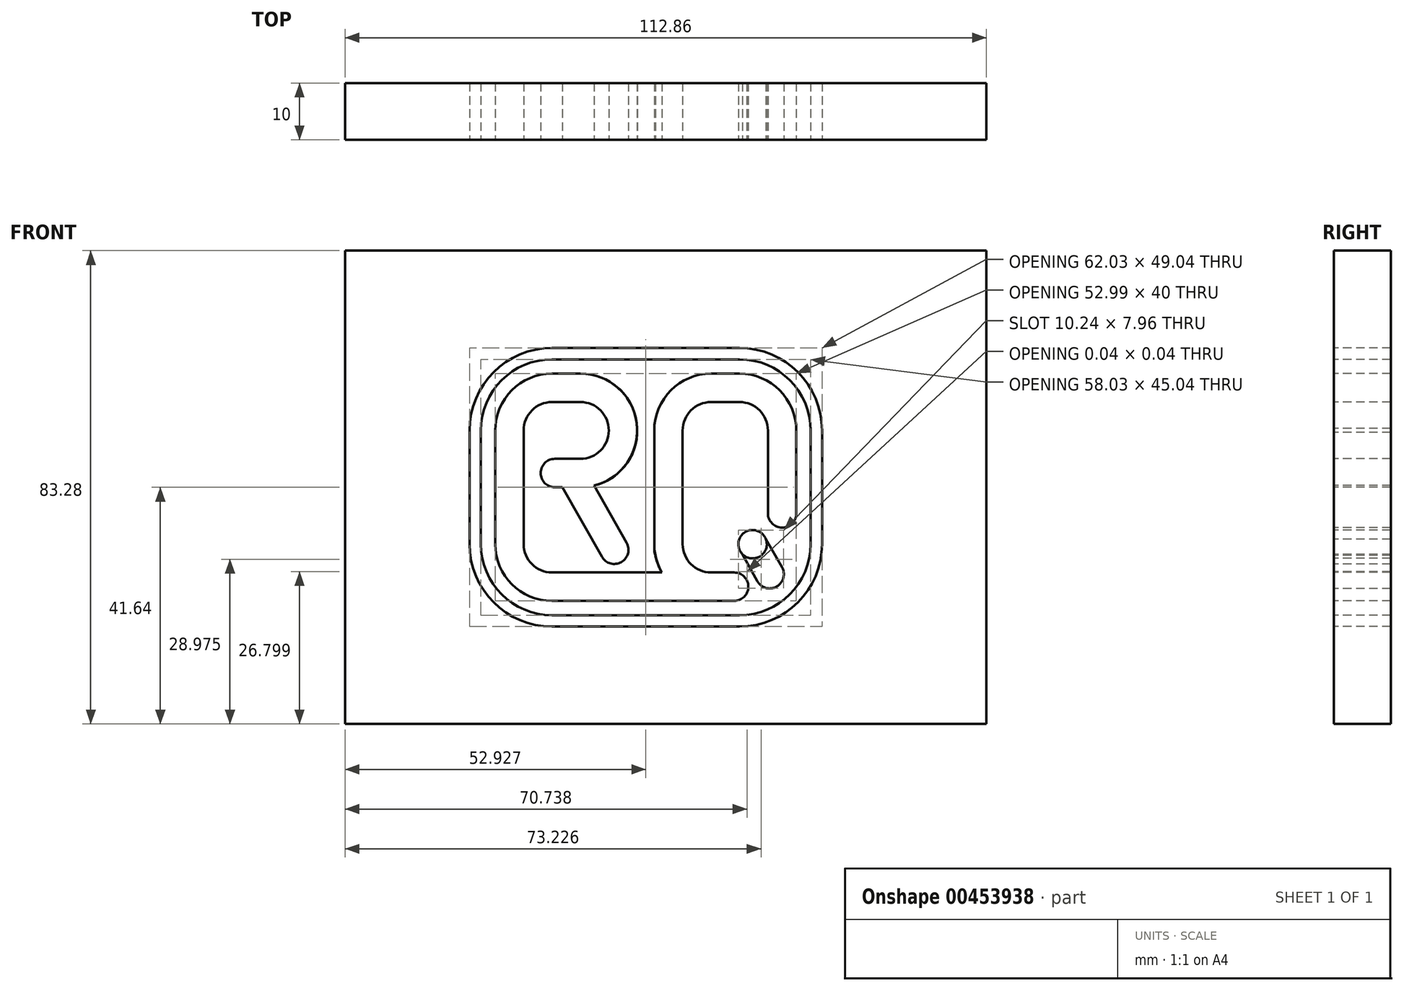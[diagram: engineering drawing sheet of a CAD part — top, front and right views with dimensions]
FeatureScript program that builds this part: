
annotation { "Feature Type Name" : "Feature", "Feature Type Description" : "" }
export const myFeature = defineFeature(function(context is Context, id is Id, definition is map)
    precondition{}
    {
        {
            var Q0;
            Q0=qCreatedBy(makeId("Front.planeOp"),FACE);
            var sketch = newSketch(context, id + "F0", { "sketchPlane" : qUnion([Q0])});
            skPoint(sketch, "E0.middle", {"position": v(0, 0) * mm});
            skLineSegment(sketch, "E1", {"start": v(-25, 10) * mm, "end": v(-25, -10) * mm});
            skLineSegment(sketch, "E2", {"start": v(-2, -20) * mm, "end": v(-0.38, -20) * mm});
            skLineSegment(sketch, "E3", {"start": v(-2, -11) * mm, "end": v(-2, 10) * mm});
            skLineSegment(sketch, "E4", {"start": v(8, 20) * mm, "end": v(13, 20) * mm});
            skLineSegment(sketch, "E5", {"start": v(23, 10) * mm, "end": v(23, -10) * mm});
            skLineSegment(sketch, "E6", {"start": v(13, -20) * mm, "end": v(9, -20) * mm});
            skLineSegment(sketch, "E7", {"start": v(-25, 20) * mm, "end": v(-15, 20) * mm});
            skLineSegment(sketch, "E8", {"start": v(-19.5, 0) * mm, "end": v(-15, 0) * mm});
            skLineSegment(sketch, "E9", {"start": v(-5, 10.33) * mm, "end": v(-5, 10.33) * mm});
            skPoint(sketch, "E10.visualSharp", {"position": v(-5.33, 20) * mm});
            skArc(sketch, "E10.filletArc", {"start": v(-5, 10.33) * mm, "mid": v(-8.05, 17.19) * mm, "end": v(-15, 20) * mm});
            skArc(sketch, "E11.filletArc", {"start": v(-15, 0) * mm, "mid": v(-7.81, 3.05) * mm, "end": v(-5, 10.33) * mm});
            skPoint(sketch, "E12.visualSharp", {"position": v(-3.63, -20) * mm});
            skPoint(sketch, "E13.visualSharp", {"position": v(23, -20) * mm});
            skPoint(sketch, "E14.visualSharp", {"position": v(23, 20) * mm});
            skArc(sketch, "E14.filletArc", {"start": v(23, 10) * mm, "mid": v(20.07, 17.07) * mm, "end": v(13, 20) * mm});
            skPoint(sketch, "E15.visualSharp", {"position": v(-2, 20) * mm});
            skArc(sketch, "E15.filletArc", {"start": v(8, 20) * mm, "mid": v(0.92, 17.07) * mm, "end": v(-2, 10) * mm});
            skPoint(sketch, "E16.visualSharp", {"position": v(-2, -20) * mm});
            skArc(sketch, "E17.0", {"start": v(8, 15) * mm, "mid": v(4.46, 13.54) * mm, "end": v(3, 10) * mm});
            skLineSegment(sketch, "E17.1", {"start": v(3, -11) * mm, "end": v(3, 10) * mm});
            skLineSegment(sketch, "E17.2", {"start": v(8, 15) * mm, "end": v(13, 15) * mm});
            skArc(sketch, "E17.4", {"start": v(18, 10) * mm, "mid": v(16.53, 13.54) * mm, "end": v(13, 15) * mm});
            skLineSegment(sketch, "E17.5", {"start": v(18, 10) * mm, "end": v(18, -10) * mm});
            skArc(sketch, "E17.6", {"start": v(14.29, -14.83) * mm, "mid": v(14.3, -14.82) * mm, "end": v(14.33, -14.82) * mm});
            skLineSegment(sketch, "E17.7", {"start": v(13, -15) * mm, "end": v(9, -15) * mm});
            skArc(sketch, "E18.1", {"start": v(-15, 5) * mm, "mid": v(-11.44, 6.5) * mm, "end": v(-10, 10.08) * mm});
            skArc(sketch, "E18.2", {"start": v(-10, 10.08) * mm, "mid": v(-11.5, 13.56) * mm, "end": v(-15, 15) * mm});
            skLineSegment(sketch, "E18.3", {"start": v(-20, 15) * mm, "end": v(-15, 15) * mm});
            skLineSegment(sketch, "E19.0", {"start": v(-30, 17.5) * mm, "end": v(-30, -10) * mm});
            skLineSegment(sketch, "E20.0", {"start": v(-1, -15) * mm, "end": v(-0.38, -15) * mm});
            skLineSegment(sketch, "E21", {"start": v(-20, -20) * mm, "end": v(-2, -20) * mm});
            skLineSegment(sketch, "E22", {"start": v(-1, -15) * mm, "end": v(0, -15) * mm});
            skLineSegment(sketch, "E23.0", {"start": v(-20, -15) * mm, "end": v(0, -15) * mm});
            skLineSegment(sketch, "E24", {"start": v(-5, 10.33) * mm, "end": v(-5, 0) * mm});
            skLineSegment(sketch, "E25", {"start": v(0.5, -13.5) * mm, "end": v(0.5, -13.5) * mm});
            skPoint(sketch, "E26.visualSharp", {"position": v(3, -13.5) * mm});
            skArc(sketch, "E26.filletArc", {"start": v(0.5, -13.5) * mm, "mid": v(2.26, -12.77) * mm, "end": v(3, -11) * mm, "construction": true});
            skPoint(sketch, "E27.newPointB", {"position": v(-23.5, -13.5) * mm});
            skArc(sketch, "E27.filletArc", {"start": v(-2, -11) * mm, "mid": v(-1.27, -12.77) * mm, "end": v(0.5, -13.5) * mm});
            skPoint(sketch, "E28.visualSharp", {"position": v(-30, -20) * mm});
            skArc(sketch, "E28.filletArc", {"start": v(-30, -19.5) * mm, "mid": v(-29.85, -19.85) * mm, "end": v(-29.5, -20) * mm});
            skLineSegment(sketch, "E29", {"start": v(-7.28, -12.77) * mm, "end": v(-7.28, -12.77) * mm});
            skArc(sketch, "E30.filletArc", {"start": v(-7.28, -12.77) * mm, "mid": v(-6.55, -11) * mm, "end": v(-7.27, -9.24) * mm});
            skArc(sketch, "E31.filletArc", {"start": v(-11.23, -12.21) * mm, "mid": v(-9.4, -13.48) * mm, "end": v(-7.28, -12.77) * mm});
            skLineSegment(sketch, "E32.0", {"start": v(14.32, -14.86) * mm, "end": v(14.29, -14.83) * mm});
            skPoint(sketch, "E33.newPointB", {"position": v(-25, 20) * mm});
            skPoint(sketch, "E34.visualSharp", {"position": v(-23.5, 5) * mm});
            skPoint(sketch, "E35.visualSharp", {"position": v(-23.5, 0) * mm});
            skLineSegment(sketch, "E36", {"start": v(-30, 10) * mm, "end": v(-30, 17.5) * mm});
            skLineSegment(sketch, "E37", {"start": v(-20, 20) * mm, "end": v(-25, 20) * mm});
            skPoint(sketch, "E38.visualSharp", {"position": v(-30, 20) * mm});
            skArc(sketch, "E38.filletArc", {"start": v(-20, 20) * mm, "mid": v(-27.07, 17.07) * mm, "end": v(-30, 10) * mm});
            skPoint(sketch, "E39", {"position": v(19.6, -17.6) * mm});
            skPoint(sketch, "E40.orphan", {"position": v(17, -13) * mm});
            skLineSegment(sketch, "E41.trimOffspring", {"start": v(13, -20) * mm, "end": v(-0.38, -20) * mm});
            skPoint(sketch, "E42.newPointB", {"position": v(-25, -20) * mm});
            skArc(sketch, "E42.filletArc", {"start": v(-25, -10) * mm, "mid": v(-23.54, -13.54) * mm, "end": v(-20, -15) * mm});
            skLineSegment(sketch, "E43", {"start": v(-15, 20) * mm, "end": v(8, 20) * mm});
            skLineSegment(sketch, "E44", {"start": v(21.86, -24.52) * mm, "end": v(-20, -24.52) * mm});
            skLineSegment(sketch, "E45", {"start": v(27.51, -22.02) * mm, "end": v(27.51, -18.86) * mm});
            skLineSegment(sketch, "E46", {"start": v(13, 24.52) * mm, "end": v(-20, 24.52) * mm});
            skLineSegment(sketch, "E47", {"start": v(-34.52, -10) * mm, "end": v(-34.52, 10) * mm});
            skPoint(sketch, "E48.orphan", {"position": v(17.43, -17.97) * mm});
            skPoint(sketch, "E49.orphan", {"position": v(13.35, -13.89) * mm});
            skArc(sketch, "E50.0", {"start": v(27.51, 10) * mm, "mid": v(23.26, 20.27) * mm, "end": v(13, 24.52) * mm});
            skArc(sketch, "E51.0", {"start": v(25.51, 10) * mm, "mid": v(21.85, 18.85) * mm, "end": v(13, 22.52) * mm});
            skLineSegment(sketch, "E52.0", {"start": v(25.51, -22.07) * mm, "end": v(25.51, -18.99) * mm});
            skLineSegment(sketch, "E53.0", {"start": v(25.02, -22.52) * mm, "end": v(21.98, -22.52) * mm});
            skLineSegment(sketch, "E54.0", {"start": v(-32.52, -10) * mm, "end": v(-32.52, 10) * mm});
            skLineSegment(sketch, "E55.0", {"start": v(13, 22.52) * mm, "end": v(-20, 22.52) * mm});
            skPoint(sketch, "E56.visualSharp", {"position": v(-32.52, 22.52) * mm});
            skArc(sketch, "E56.filletArc", {"start": v(-20, 22.52) * mm, "mid": v(-28.85, 18.85) * mm, "end": v(-32.52, 10) * mm});
            skArc(sketch, "E57.0", {"start": v(-20, 24.52) * mm, "mid": v(-30.27, 20.27) * mm, "end": v(-34.52, 10) * mm});
            skPoint(sketch, "E58.visualSharp", {"position": v(-32.52, -22.52) * mm});
            skLineSegment(sketch, "E59", {"start": v(26.51, -15) * mm, "end": v(26.51, -16.32) * mm});
            skLineSegment(sketch, "E60.0", {"start": v(18.1, -20.77) * mm, "end": v(22.19, -24.85) * mm, "construction": true});
            skLineSegment(sketch, "E61.0", {"start": v(23.76, -15.1) * mm, "end": v(27.84, -19.2) * mm, "construction": true});
            skLineSegment(sketch, "E62.trimOffspring", {"start": v(25.51, -14) * mm, "end": v(25.51, 10) * mm});
            skLineSegment(sketch, "E63.trimOffspring", {"start": v(27.51, -14) * mm, "end": v(27.51, 33) * mm});
            skLineSegment(sketch, "E64.trimOffspring", {"start": v(19.86, -22.52) * mm, "end": v(-20, -22.52) * mm});
            skLineSegment(sketch, "E65", {"start": v(21.86, -24.52) * mm, "end": v(25.02, -24.52) * mm});
            skLineSegment(sketch, "E66", {"start": v(27.51, -14) * mm, "end": v(27.51, -22.02) * mm});
            skLineSegment(sketch, "E67.bottom", {"start": v(-56.43, 41.64) * mm, "end": v(56.43, 41.64) * mm});
            skLineSegment(sketch, "E67.top", {"start": v(-56.43, -41.64) * mm, "end": v(56.43, -41.64) * mm});
            skLineSegment(sketch, "E67.left", {"start": v(-56.43, 41.64) * mm, "end": v(-56.43, -41.64) * mm});
            skLineSegment(sketch, "E67.right", {"start": v(56.43, 41.64) * mm, "end": v(56.43, -41.64) * mm});
            skLineSegment(sketch, "E68", {"start": v(0, 0) * mm, "end": v(0, -38.7) * mm, "construction": true});
            skLineSegment(sketch, "E69", {"start": v(0, 0) * mm, "end": v(33.56, 0) * mm, "construction": true});
            skArc(sketch, "E70.filletArc", {"start": v(-20, 15) * mm, "mid": v(-23.54, 13.54) * mm, "end": v(-25, 10) * mm});
            skArc(sketch, "E71.0", {"start": v(-30, -10) * mm, "mid": v(-27.07, -17.07) * mm, "end": v(-20, -20) * mm});
            skArc(sketch, "E72.0", {"start": v(-34.52, -10) * mm, "mid": v(-30.27, -20.27) * mm, "end": v(-20, -24.52) * mm});
            skArc(sketch, "E73.0", {"start": v(-32.52, -10) * mm, "mid": v(-28.85, -18.85) * mm, "end": v(-20, -22.52) * mm});
            skLineSegment(sketch, "E74", {"start": v(-15, 5) * mm, "end": v(-19.5, 5) * mm});
            skLineSegment(sketch, "E75", {"start": v(-23.5, 2.5) * mm, "end": v(-23.5, 2.5) * mm});
            skArc(sketch, "E76.filletArc", {"start": v(-21, 5) * mm, "mid": v(-22.77, 4.27) * mm, "end": v(-23.5, 2.5) * mm, "construction": true});
            skArc(sketch, "E77.filletArc", {"start": v(-23.5, 2.5) * mm, "mid": v(-22.77, 0.73) * mm, "end": v(-21, 0) * mm, "construction": true});
            skPoint(sketch, "E78.startSnap0", {"position": v(-6.55, -11) * mm});
            skLineSegment(sketch, "E79", {"start": v(-22.87, 0.84) * mm, "end": v(-10.92, -12.66) * mm, "construction": true});
            skLineSegment(sketch, "E80.0", {"start": v(-19.13, 4.16) * mm, "end": v(-7.17, -9.34) * mm, "construction": true});
            skArc(sketch, "E81.0", {"start": v(13, -22.52) * mm, "mid": v(21.85, -18.85) * mm, "end": v(25.51, -10) * mm});
            skArc(sketch, "E82.0", {"start": v(13, -24.52) * mm, "mid": v(23.26, -20.27) * mm, "end": v(27.51, -10) * mm});
            skCircle(sketch, "E83", {"center": v(18.3, -15.3) * mm, "radius": 2.5 * mm});
            skLineSegment(sketch, "E84", {"start": v(-21, 5) * mm, "end": v(-21, 0) * mm, "construction": true});
            skLineSegment(sketch, "E85", {"start": v(-21, 5) * mm, "end": v(-11.1, -12.46) * mm});
            skLineSegment(sketch, "E86.0", {"start": v(-16.65, 7.47) * mm, "end": v(-6.74, -10) * mm});
            skLineSegment(sketch, "E87", {"start": v(-22, 7.3) * mm, "end": v(-22, -4.59) * mm});
            skLineSegment(sketch, "E88", {"start": v(-28.56, 2.5) * mm, "end": v(-6.16, 2.5) * mm, "construction": true});
            skCircle(sketch, "E89", {"center": v(-19.5, 2.5) * mm, "radius": 2.5 * mm});
            skLineSegment(sketch, "E90", {"start": v(17, -13) * mm, "end": v(19.6, -17.6) * mm});
            skArc(sketch, "E91.0", {"start": v(14.33, -14.82) * mm, "mid": v(14.32, -14.84) * mm, "end": v(14.32, -14.86) * mm});
            skLineSegment(sketch, "E92", {"start": v(10.5, 15) * mm, "end": v(10.5, 5.39) * mm, "construction": true});
            skArc(sketch, "E93.MirrorCS", {"start": v(8, -15) * mm, "mid": v(4.46, -13.54) * mm, "end": v(3, -10) * mm});
            skArc(sketch, "E94.MirrorCS", {"start": v(8, -20) * mm, "mid": v(0.92, -17.07) * mm, "end": v(-2, -10) * mm});
            skLineSegment(sketch, "E95.trimOffspring", {"start": v(8, -15) * mm, "end": v(9, -15) * mm});
            skArc(sketch, "E96", {"start": v(12.04, -20) * mm, "mid": v(14.54, -17.5) * mm, "end": v(12.04, -15) * mm});
            skArc(sketch, "E97", {"start": v(18, -4.59) * mm, "mid": v(20.5, -7.09) * mm, "end": v(23, -4.59) * mm});
            skLineSegment(sketch, "E98", {"start": v(18.3, -15.3) * mm, "end": v(13.06, -6.07) * mm});
            skCircle(sketch, "E99", {"center": v(15.3, -10.02) * mm, "radius": 2.5 * mm});
            skLineSegment(sketch, "E100", {"start": v(17.26, -8.46) * mm, "end": v(20.47, -14.06) * mm});
            skLineSegment(sketch, "E101", {"start": v(13.53, -11.79) * mm, "end": v(16.1, -16.5) * mm});
            skSolve(sketch);
        }
        {
            var Q0;
            Q0=makeQuery(id+"F0.imprint","IMPRINT",FACE,{"disambiguationData":[TD([[makeQuery(id+"F0.imprint","IMPRINT",EDGE,{"derivedFrom":sQuery(id+"F0.wireOp",EDGE,"E1")}),-1.0]])]});
            var Q1;
            {var subQ6=sQuery(id+"F0.wireOp",EDGE,"8dgEX87s-OnN3-UPAw-RyUf-tcfM0RuKeMZf");Q1=makeQuery(id+"F0.imprint","IMPRINT",FACE,{"disambiguationData":[TD([[makeQuery(id+"F0.imprint","IMPRINT",EDGE,{"derivedFrom":subQ6}),1.0]])]});}
            var Q2;
            {var subQ0=sQuery(id+"F0.wireOp",EDGE,"S70SFG3v-wlmV-iE8w-7gkR-MiBzXbBwRlH9");var subQ1=makeQuery(id+"F0.imprint","INTERSECT",VERTEX,{"derivedFrom":[sQuery(id+"F0.wireOp",EDGE,"c0c087a9-fd36-4214-a694-875f0f01d769.0"),subQ0]});Q2=makeQuery(id+"F0.imprint","IMPRINT",FACE,{"disambiguationData":[TD([[makeQuery(id+"F0.imprint","IMPRINT",EDGE,{"disambiguationData":[TD([[subQ1,-1.0]])],"derivedFrom":subQ0}),1.0]])]});}
            var Q3;
            {var subQ1=sQuery(id+"F0.wireOp",EDGE,"c0c087a9-fd36-4214-a694-875f0f01d769.0");Q3=makeQuery(id+"F0.imprint","IMPRINT",FACE,{"disambiguationData":[TD([[makeQuery(id+"F0.imprint","IMPRINT",EDGE,{"derivedFrom":subQ1}),-1.0]])]});}
            var Q4;
            {var subQ0=sQuery(id+"F0.wireOp",EDGE,"E0.bottom");Q4=makeQuery(id+"F0.imprint","IMPRINT",FACE,{"disambiguationData":[TD([[makeQuery(id+"F0.imprint","IMPRINT",EDGE,{"derivedFrom":subQ0}),-1.0]])]});}
            var Q5;
            {var subQ0=sQuery(id+"F0.wireOp",EDGE,"E0.bottom");Q5=makeQuery(id+"F0.imprint","IMPRINT",FACE,{"disambiguationData":[TD([[makeQuery(id+"F0.imprint","IMPRINT",EDGE,{"derivedFrom":subQ0}),1.0]])]});}
            var Q6;
            {var subQ3=sQuery(id+"F0.wireOp",EDGE,"E8");var subQ7=sQuery(id+"F0.wireOp",EDGE,"E11.filletArc");var subQ8=makeQuery(id+"F0.imprint","INTERSECT",VERTEX,{"derivedFrom":[subQ3,subQ7]});Q6=makeQuery(id+"F0.imprint","IMPRINT",FACE,{"disambiguationData":[TD([[makeQuery(id+"F0.imprint","IMPRINT",EDGE,{"disambiguationData":[TD([[subQ8,1.0]])],"derivedFrom":subQ3}),1.0]])]});}
            var Q7;
            {var subQ4=sQuery(id+"F0.wireOp",EDGE,"E76.filletArc");Q7=makeQuery(id+"F0.imprint","IMPRINT",FACE,{"disambiguationData":[TD([[makeQuery(id+"F0.imprint","IMPRINT",EDGE,{"derivedFrom":subQ4}),1.0]])]});}
            var Q8;
            {var subQ0=sQuery(id+"F0.wireOp",EDGE,"E31.filletArc");Q8=makeQuery(id+"F0.imprint","IMPRINT",FACE,{"disambiguationData":[TD([[makeQuery(id+"F0.imprint","IMPRINT",EDGE,{"derivedFrom":subQ0}),1.0]])]});}
            var Q9;
            Q9=makeQuery(id+"F0.imprint","IMPRINT",FACE,{"disambiguationData":[TD([[makeQuery(id+"F0.imprint","IMPRINT",EDGE,{"derivedFrom":sQuery(id+"F0.wireOp",EDGE,"E83")}),1.0]])]});
            var Q10;
            {var subQ0=sQuery(id+"F0.wireOp",EDGE,"E88");var subQ1=sQuery(id+"F0.wireOp",EDGE,"E11.filletArc");var subQ2=makeQuery(id+"F0.imprint","INTERSECT",VERTEX,{"derivedFrom":[subQ1,subQ0]});Q10=makeQuery(id+"F0.imprint","IMPRINT",FACE,{"disambiguationData":[TD([[makeQuery(id+"F0.imprint","IMPRINT",EDGE,{"disambiguationData":[TD([[subQ2,1.0]])],"derivedFrom":subQ1}),1.0]])]});}
            var Q11;
            {var subQ0=sQuery(id+"F0.wireOp",EDGE,"E89");var subQ1=sQuery(id+"F0.wireOp",EDGE,"E74");var subQ2=makeQuery(id+"F0.imprint","INTERSECT",VERTEX,{"derivedFrom":[subQ1,subQ0]});Q11=makeQuery(id+"F0.imprint","IMPRINT",FACE,{"disambiguationData":[TD([[makeQuery(id+"F0.imprint","IMPRINT",EDGE,{"disambiguationData":[TD([[subQ2,1.0]])],"derivedFrom":subQ1}),1.0]])]});}
            var Q12;
            {var subQ0=sQuery(id+"F0.wireOp",EDGE,"E88");var subQ1=sQuery(id+"F0.wireOp",EDGE,"E85");var subQ2=makeQuery(id+"F0.imprint","INTERSECT",VERTEX,{"derivedFrom":[subQ1,subQ0]});Q12=makeQuery(id+"F0.imprint","IMPRINT",FACE,{"disambiguationData":[TD([[makeQuery(id+"F0.imprint","IMPRINT",EDGE,{"disambiguationData":[TD([[subQ2,-1.0]])],"derivedFrom":subQ1}),-1.0]])]});}
            var Q13;
            {var subQ0=sQuery(id+"F0.wireOp",EDGE,"E89");var subQ1=sQuery(id+"F0.wireOp",EDGE,"E85");var subQ2=makeQuery(id+"F0.imprint","INTERSECT",VERTEX,{"disambiguationData":[OD(0.0)],"derivedFrom":[subQ1,subQ0]});Q13=makeQuery(id+"F0.imprint","IMPRINT",FACE,{"disambiguationData":[TD([[makeQuery(id+"F0.imprint","IMPRINT",EDGE,{"disambiguationData":[TD([[subQ2,-1.0]])],"derivedFrom":subQ1}),-1.0]])]});}
            var Q14;
            {var subQ0=sQuery(id+"F0.wireOp",EDGE,"E89");var subQ1=sQuery(id+"F0.wireOp",EDGE,"E85");var subQ2=makeQuery(id+"F0.imprint","INTERSECT",VERTEX,{"disambiguationData":[OD(0.0)],"derivedFrom":[subQ1,subQ0]});Q14=makeQuery(id+"F0.imprint","IMPRINT",FACE,{"disambiguationData":[TD([[makeQuery(id+"F0.imprint","IMPRINT",EDGE,{"disambiguationData":[TD([[subQ2,-1.0]])],"derivedFrom":subQ1}),1.0]])]});}
            var Q15;
            {var subQ0=sQuery(id+"F0.wireOp",EDGE,"E88");var subQ1=sQuery(id+"F0.wireOp",EDGE,"E85");var subQ2=makeQuery(id+"F0.imprint","INTERSECT",VERTEX,{"derivedFrom":[subQ1,subQ0]});Q15=makeQuery(id+"F0.imprint","IMPRINT",FACE,{"disambiguationData":[TD([[makeQuery(id+"F0.imprint","IMPRINT",EDGE,{"disambiguationData":[TD([[subQ2,-1.0]])],"derivedFrom":subQ1}),1.0]])]});}
            var Q16;
            {var subQ0=sQuery(id+"F0.wireOp",EDGE,"E89");var subQ1=sQuery(id+"F0.wireOp",EDGE,"E8");var subQ2=makeQuery(id+"F0.imprint","INTERSECT",VERTEX,{"derivedFrom":[subQ1,subQ0]});Q16=makeQuery(id+"F0.imprint","IMPRINT",FACE,{"disambiguationData":[TD([[makeQuery(id+"F0.imprint","IMPRINT",EDGE,{"disambiguationData":[TD([[subQ2,-1.0]])],"derivedFrom":subQ1}),1.0]])]});}
            var Q17;
            Q17=makeQuery(id+"F0.imprint","IMPRINT",FACE,{"disambiguationData":[TD([[makeQuery(id+"F0.imprint","IMPRINT",EDGE,{"derivedFrom":sQuery(id+"F0.wireOp",EDGE,"E4")}),-1.0]])]});
            var Q18;
            {var subQ0=sQuery(id+"F0.wireOp",EDGE,"E99");var subQ1=sQuery(id+"F0.wireOp",EDGE,"E98");var subQ2=makeQuery(id+"F0.imprint","INTERSECT",VERTEX,{"disambiguationData":[OD(0.0)],"derivedFrom":[subQ1,subQ0]});Q18=makeQuery(id+"F0.imprint","IMPRINT",FACE,{"disambiguationData":[TD([[makeQuery(id+"F0.imprint","IMPRINT",EDGE,{"disambiguationData":[TD([[subQ2,1.0]])],"derivedFrom":subQ1}),-1.0]])]});}
            var Q19;
            {var subQ0=sQuery(id+"F0.wireOp",EDGE,"E99");var subQ1=sQuery(id+"F0.wireOp",EDGE,"E98");var subQ2=makeQuery(id+"F0.imprint","INTERSECT",VERTEX,{"disambiguationData":[OD(0.0)],"derivedFrom":[subQ1,subQ0]});Q19=makeQuery(id+"F0.imprint","IMPRINT",FACE,{"disambiguationData":[TD([[makeQuery(id+"F0.imprint","IMPRINT",EDGE,{"disambiguationData":[TD([[subQ2,1.0]])],"derivedFrom":subQ1}),1.0]])]});}
            var Q20;
            {var subQ0=sQuery(id+"F0.wireOp",EDGE,"E100");Q20=makeQuery(id+"F0.imprint","IMPRINT",FACE,{"disambiguationData":[TD([[makeQuery(id+"F0.imprint","IMPRINT",EDGE,{"derivedFrom":subQ0}),-1.0]])]});}
            var Q21;
            {var subQ4=sQuery(id+"F0.wireOp",EDGE,"E101");Q21=makeQuery(id+"F0.imprint","IMPRINT",FACE,{"disambiguationData":[TD([[makeQuery(id+"F0.imprint","IMPRINT",EDGE,{"derivedFrom":subQ4}),1.0]])]});}
            extrude(context, id + "F1", {"entities" : qUnion([Q0, Q1, Q2, Q3, Q4, Q5, Q6, Q7, Q8, Q9, Q10, Q11, Q12, Q13, Q14, Q15, Q16, Q17, Q18, Q19, Q20, Q21]), "oppositeDirection" : true, "depth" : 10 * mm});
        }
        {
            var Q0;
            Q0=makeQuery(id+"F0.imprint","IMPRINT",FACE,{"disambiguationData":[TD([[makeQuery(id+"F0.imprint","IMPRINT",EDGE,{"derivedFrom":sQuery(id+"F0.wireOp",EDGE,"E1")}),1.0]])]});
            var Q1;
            {var subQ16=sQuery(id+"F0.wireOp",EDGE,"E2");Q1=makeQuery(id+"F0.imprint","IMPRINT",FACE,{"disambiguationData":[TD([[makeQuery(id+"F0.imprint","IMPRINT",EDGE,{"derivedFrom":subQ16}),-1.0]])]});}
            extrude(context, id + "F2", {"entities" : qUnion([Q0, Q1]), "oppositeDirection" : true, "depth" : 10 * mm});
        }
        {
            var Q0;
            Q0=makeQuery(id+"F0.imprint","IMPRINT",FACE,{"disambiguationData":[TD([[makeQuery(id+"F0.imprint","IMPRINT",EDGE,{"derivedFrom":sQuery(id+"F0.wireOp",EDGE,"E46")}),1.0]])]});
            var Q1;
            {var subQ0=sQuery(id+"F0.wireOp",EDGE,"aTrX08yB-o83u-csdW-HvKf-6qn933KxLSEO");var subQ2=makeQuery(id+"F0.imprint","IMPRINT",VERTEX,{"derivedFrom":subQ0});Q1=makeQuery(id+"F0.imprint","IMPRINT",FACE,{"disambiguationData":[TD([[makeQuery(id+"F0.imprint","IMPRINT",EDGE,{"disambiguationData":[TD([[subQ2,-1.0]])],"derivedFrom":subQ0}),1.0]])]});}
            var Q2;
            {var subQ0=sQuery(id+"F0.wireOp",EDGE,"orb3SBHr-i0Mj-h6B2-otKM-5Ab6eh35dINg");var subQ3=makeQuery(id+"F0.imprint","IMPRINT",VERTEX,{"derivedFrom":subQ0});Q2=makeQuery(id+"F0.imprint","IMPRINT",FACE,{"disambiguationData":[TD([[makeQuery(id+"F0.imprint","IMPRINT",EDGE,{"disambiguationData":[TD([[subQ3,1.0]])],"derivedFrom":subQ0}),1.0]])]});}
            extrude(context, id + "F3", {"entities" : qUnion([Q0, Q1, Q2]), "oppositeDirection" : true, "depth" : 10 * mm});
        }
        {
            var Q0;
            Q0=makeQuery(id+"F0.imprint","IMPRINT",FACE,{"disambiguationData":[TD([[makeQuery(id+"F0.imprint","IMPRINT",EDGE,{"derivedFrom":sQuery(id+"F0.wireOp",EDGE,"E46")}),-1.0]])]});
            extrude(context, id + "F4", {"entities" : qUnion([Q0]), "oppositeDirection" : true, "depth" : 10 * mm});
        }
    });
